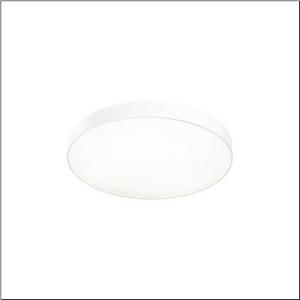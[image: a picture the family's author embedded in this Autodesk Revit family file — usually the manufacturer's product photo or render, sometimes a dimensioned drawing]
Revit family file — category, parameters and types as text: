
# Revit family: round_21_m_51mr36gm8421w
name_source: partatom
category: Lighting Fixtures
units: mm (PartAtom-declared; Revit-internal decimal feet)

## family parameters
Cut with Voids When Loaded = No
Host = Face
Light Source = No
Part Type = Normal
Room Calculation Point = No
Round Connector Dimension = Use Diameter
Shared = No

## types (1)
- --- (1 x LED, 8960 lm, 62.3 W, 4000K)
    Apparent Load = 62 VA
    CIE Flux Codes = 49 80 96 85 100
    Color Rendering = 80
    Color Temperature = 4000K
    Default Elevation = 1800 mm
    Description = Round 21 M, wall and ceiling luminaire, primary optical cover: cover, of PMMA, opal, light emission: direct/indirect distribution, primary light characteristic: symmetric, installation type: suspended mounting, surface-mounted, LED, rated luminous flux: 8.190lm, luminous efficacy: 135lm/W, light colour: 840, colour temperature: 4000K, control gear: ON/OFF Multilumen, with terminal, 3-pole, mains connection: 230V, AC, 50/60Hz, rated input power: 61W, housing, of aluminium, coated, white, diameter: 600mm, height: 62mm, protection rating (complete): IP40, insulation class (complete): insulation class I (protective earthing), certification: CE, impact resistance: IK04, permissible operating ambient temperature: -10..+35°C, packaging unit: 1 piece
    Height = 87 mm
    Lamp = 1 x LED
    Lamp Light Flux = 8960 lm
    Lamp Power = 62.3 W
    Lamp count = 1
    Length = 600 mm
    Luminous efficacy = 144 lm/W
    Manufacturer = Siteco
    ModVariant = No
    Model = 51MR36GM8421W
    Mounting Place = Ceiling
    Mounting Type = Surface mounted
    Number of Poles = 1
    OnlyDefault = Yes
    Power Factor = 1
    Product Name = Round 21 M
    Product group = wall and ceiling luminaire
    ProductGroupID = 304
    Protection Class = Protection class I
    Protection Degree = IP 40
    RLX_Detail_Level = 1
    RLX_Emergency_Light_Flux = 0 lm
    RLX_Emergency_Type = 0
    RLX_Emergency_Type_DB = No
    RlxData = <blob elided: 14813 chars, md5=3e333756>
    Socket = socket
    Standby Power = 0 W
    System Light Flux = 8960 lm
    System Power = 62 W
    Type Comments = factory setting: luminous flux: 100 % | (ON | ON | ON | ON) | 700 mA
    Type Image = l_1258330.jpg
    URL = http://relux.com
    VarID = @adj_032750
    Voltage = 0 V
    Weight = 0.00 kg
    Width = 0 mm  [stored 0 ft]

note: [stored X ft] marks values corroborated as IEEE doubles in the binary element streams (Revit-internal decimal feet)

## geometry (parser evidence)
native form markers: Sweep x13
no freeform markers — native parametric forms only
